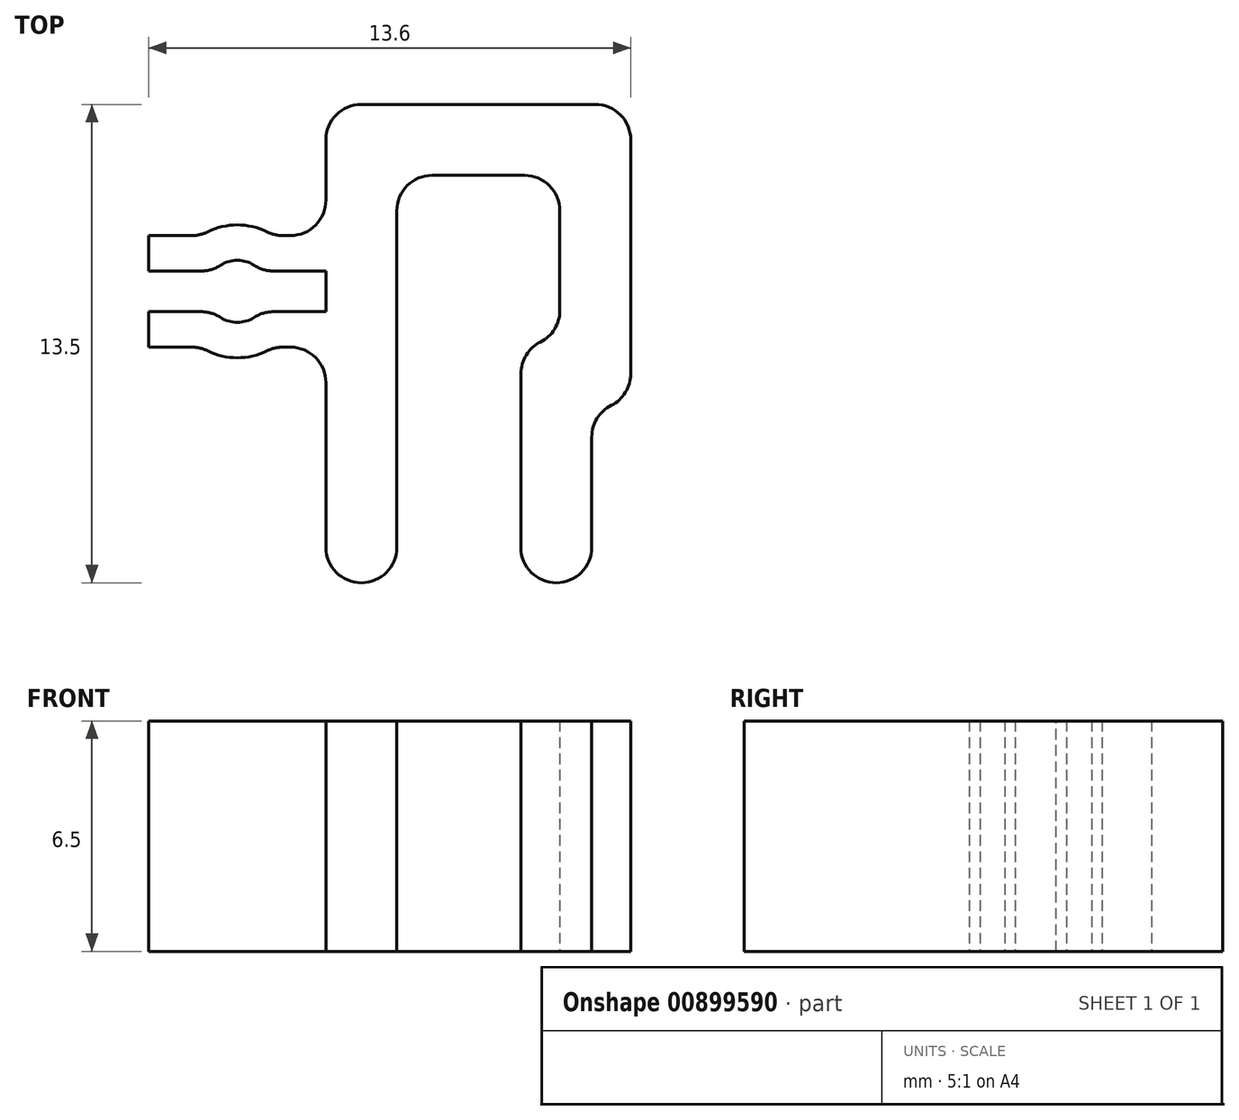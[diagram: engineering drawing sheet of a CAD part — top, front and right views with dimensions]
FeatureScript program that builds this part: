
annotation { "Feature Type Name" : "Feature", "Feature Type Description" : "" }
export const myFeature = defineFeature(function(context is Context, id is Id, definition is map)
    precondition{}
    {
        {
            var Q0;
            Q0=qCreatedBy(makeId("Top.planeOp"),FACE);
            var sketch = newSketch(context, id + "F0", { "sketchPlane" : qUnion([Q0])});
            skLineSegment(sketch, "E0.bottom", {"start": v(2.3, 2.3) * mm, "end": v(-2.3, 2.3) * mm});
            skLineSegment(sketch, "E0.left", {"start": v(2.3, 2.3) * mm, "end": v(2.3, -2.3) * mm});
            skLineSegment(sketch, "E0.right", {"start": v(-2.3, 2.3) * mm, "end": v(-2.3, -2.3) * mm});
            skPoint(sketch, "E0.middle", {"position": v(0, 0) * mm});
            skLineSegment(sketch, "E1.0", {"start": v(4.3, 4.3) * mm, "end": v(-4.3, 4.3) * mm});
            skLineSegment(sketch, "E1.1", {"start": v(4.3, 4.3) * mm, "end": v(4.3, -4.3) * mm});
            skLineSegment(sketch, "E2.0", {"start": v(-4.3, 4.3) * mm, "end": v(-4.3, -2.3) * mm});
            skLineSegment(sketch, "E3", {"start": v(2.3, -2.3) * mm, "end": v(1.2, -2.3) * mm});
            skLineSegment(sketch, "E4", {"start": v(1.2, -2.3) * mm, "end": v(1.2, -9.2) * mm});
            skLineSegment(sketch, "E5.0", {"start": v(3.2, -4.3) * mm, "end": v(3.2, -9.2) * mm});
            skLineSegment(sketch, "E6.0", {"start": v(4.3, -4.3) * mm, "end": v(3.2, -4.3) * mm});
            skLineSegment(sketch, "E7", {"start": v(1.2, -9.2) * mm, "end": v(3.2, -9.2) * mm});
            skLineSegment(sketch, "E8", {"start": v(-2.3, -2.3) * mm, "end": v(-2.3, -9.2) * mm});
            skLineSegment(sketch, "E9", {"start": v(-2.3, -9.2) * mm, "end": v(-4.3, -9.2) * mm});
            skLineSegment(sketch, "E10", {"start": v(-4.3, -9.2) * mm, "end": v(-4.3, -2.3) * mm});
            skLineSegment(sketch, "E11", {"start": v(-4.3, 0.6) * mm, "end": v(-5.78, 0.6) * mm});
            skLineSegment(sketch, "E12", {"start": v(-9.3, 0.6) * mm, "end": v(-9.3, -0.4) * mm});
            skLineSegment(sketch, "E13", {"start": v(-9.3, -0.4) * mm, "end": v(-7.46, -0.4) * mm});
            skLineSegment(sketch, "E14", {"start": v(-4.3, -1.55) * mm, "end": v(-6.14, -1.55) * mm});
            skLineSegment(sketch, "E15", {"start": v(-9.3, -1.55) * mm, "end": v(-9.3, -2.55) * mm});
            skLineSegment(sketch, "E16", {"start": v(-9.3, -2.55) * mm, "end": v(-4.3, -2.55) * mm});
            skLineSegment(sketch, "E17", {"start": v(-6.8, -0.4) * mm, "end": v(-6.8, -1.55) * mm, "construction": true});
            skArc(sketch, "E18", {"start": v(-7.46, -1.55) * mm, "mid": v(-6.8, -1.85) * mm, "end": v(-6.14, -1.55) * mm});
            skArc(sketch, "E19", {"start": v(-7.82, -2.55) * mm, "mid": v(-6.8, -2.85) * mm, "end": v(-5.78, -2.55) * mm});
            skArc(sketch, "E20.trimOffspring", {"start": v(-5.78, 0.6) * mm, "mid": v(-6.8, 0.9) * mm, "end": v(-7.82, 0.6) * mm});
            skLineSegment(sketch, "E21.trimOffspring", {"start": v(-7.82, 0.6) * mm, "end": v(-9.3, 0.6) * mm});
            skArc(sketch, "E22.trimOffspring", {"start": v(-6.14, -0.4) * mm, "mid": v(-6.8, -0.1) * mm, "end": v(-7.46, -0.4) * mm});
            skLineSegment(sketch, "E23.trimOffspring", {"start": v(-6.14, -0.4) * mm, "end": v(-4.3, -0.4) * mm});
            skLineSegment(sketch, "E24.trimOffspring", {"start": v(-7.46, -1.55) * mm, "end": v(-9.3, -1.55) * mm});
            skSolve(sketch);
        }
        {
            var Q0;
            Q0 = qSketchRegion(id + "F0", true);
            extrude(context, id + "F1", {"entities" : qUnion([Q0]), "depth" : 6.5 * mm, "offsetDistance" : 25.4 * mm});
        }
        {
            var Q0;
            {var subQ0=sQuery(id+"F0.wireOp",EDGE,"E19");var subQ1=sQuery(id+"F0.wireOp",EDGE,"E16");Q0=makeQuery(id+"F1.opExtrude","SWEPT_EDGE",EDGE,{"disambiguationData":[OSD([subQ1,subQ0]),TDD([makeQuery(id+"F0.imprint","INTERSECT",VERTEX,{"disambiguationData":[OD(0.0)],"derivedFrom":[subQ1,subQ0]})])]});}
            var Q1;
            {var subQ0=sQuery(id+"F0.wireOp",EDGE,"E19");var subQ1=sQuery(id+"F0.wireOp",EDGE,"E16");Q1=makeQuery(id+"F1.opExtrude","SWEPT_EDGE",EDGE,{"disambiguationData":[OSD([subQ1,subQ0]),TDD([makeQuery(id+"F0.imprint","INTERSECT",VERTEX,{"disambiguationData":[OD(1.0)],"derivedFrom":[subQ1,subQ0]})])]});}
            var Q2;
            Q2=makeQuery(id+"F1.opExtrude","SWEPT_EDGE",EDGE,{"disambiguationData":[OSD([sQuery(id+"F0.wireOp",EDGE,"E20.trimOffspring"),sQuery(id+"F0.wireOp",EDGE,"E21.trimOffspring")])]});
            var Q3;
            Q3=makeQuery(id+"F1.opExtrude","SWEPT_EDGE",EDGE,{"disambiguationData":[OSD([sQuery(id+"F0.wireOp",EDGE,"E11"),sQuery(id+"F0.wireOp",EDGE,"E20.trimOffspring")])]});
            fillet(context, id + "F2", {"entities" : qUnion([Q0, Q1, Q2, Q3]), "radius" : 1 * mm, "tangentPropagation" : true, "allowEdgeOverflow" : false});
        }
        {
            var Q0;
            Q0=makeQuery(id+"F1.opExtrude","SWEPT_EDGE",EDGE,{"disambiguationData":[OSD([sQuery(id+"F0.wireOp",EDGE,"E14"),sQuery(id+"F0.wireOp",EDGE,"E18")])]});
            var Q1;
            Q1=makeQuery(id+"F1.opExtrude","SWEPT_EDGE",EDGE,{"disambiguationData":[OSD([sQuery(id+"F0.wireOp",EDGE,"E18"),sQuery(id+"F0.wireOp",EDGE,"E24.trimOffspring")])]});
            var Q2;
            Q2=makeQuery(id+"F1.opExtrude","SWEPT_EDGE",EDGE,{"disambiguationData":[OSD([sQuery(id+"F0.wireOp",EDGE,"E13"),sQuery(id+"F0.wireOp",EDGE,"E22.trimOffspring")])]});
            var Q3;
            Q3=makeQuery(id+"F1.opExtrude","SWEPT_EDGE",EDGE,{"disambiguationData":[OSD([sQuery(id+"F0.wireOp",EDGE,"E22.trimOffspring"),sQuery(id+"F0.wireOp",EDGE,"E23.trimOffspring")])]});
            fillet(context, id + "F3", {"entities" : qUnion([Q0, Q1, Q2, Q3]), "radius" : 1 * mm, "tangentPropagation" : true, "allowEdgeOverflow" : false});
        }
        {
            var Q0;
            Q0=makeQuery(id+"F1.opExtrude","SWEPT_EDGE",EDGE,{"disambiguationData":[OSD([sQuery(id+"F0.wireOp",EDGE,"E9"),sQuery(id+"F0.wireOp",EDGE,"E10")])]});
            var Q1;
            Q1=makeQuery(id+"F1.opExtrude","SWEPT_EDGE",EDGE,{"disambiguationData":[OSD([sQuery(id+"F0.wireOp",EDGE,"E8"),sQuery(id+"F0.wireOp",EDGE,"E9")])]});
            var Q2;
            Q2=makeQuery(id+"F1.opExtrude","SWEPT_EDGE",EDGE,{"disambiguationData":[OSD([sQuery(id+"F0.wireOp",EDGE,"E4"),sQuery(id+"F0.wireOp",EDGE,"E7")])]});
            var Q3;
            Q3=makeQuery(id+"F1.opExtrude","SWEPT_EDGE",EDGE,{"disambiguationData":[OSD([sQuery(id+"F0.wireOp",EDGE,"E5.0"),sQuery(id+"F0.wireOp",EDGE,"E7")])]});
            var Q4;
            Q4=makeQuery(id+"F1.opExtrude","SWEPT_EDGE",EDGE,{"disambiguationData":[OSD([sQuery(id+"F0.wireOp",EDGE,"E1.0"),sQuery(id+"F0.wireOp",EDGE,"E2.0")])]});
            var Q5;
            Q5=makeQuery(id+"F1.opExtrude","SWEPT_EDGE",EDGE,{"disambiguationData":[OSD([sQuery(id+"F0.wireOp",EDGE,"E1.1"),sQuery(id+"F0.wireOp",EDGE,"E6.0")])]});
            var Q6;
            Q6=makeQuery(id+"F1.opExtrude","SWEPT_EDGE",EDGE,{"disambiguationData":[OSD([sQuery(id+"F0.wireOp",EDGE,"E1.0"),sQuery(id+"F0.wireOp",EDGE,"E1.1")])]});
            var Q7;
            Q7=makeQuery(id+"F1.opExtrude","SWEPT_EDGE",EDGE,{"disambiguationData":[OSD([sQuery(id+"F0.wireOp",EDGE,"E3"),sQuery(id+"F0.wireOp",EDGE,"E4")])]});
            fillet(context, id + "F4", {"entities" : qUnion([Q0, Q1, Q2, Q3, Q4, Q5, Q6, Q7]), "radius" : 1 * mm, "tangentPropagation" : true, "allowEdgeOverflow" : false});
        }
        {
            var Q0;
            Q0=makeQuery(id+"F1.opExtrude","SWEPT_EDGE",EDGE,{"disambiguationData":[OSD([sQuery(id+"F0.wireOp",EDGE,"E0.bottom"),sQuery(id+"F0.wireOp",EDGE,"E0.right")])]});
            var Q1;
            Q1=makeQuery(id+"F1.opExtrude","SWEPT_EDGE",EDGE,{"disambiguationData":[OSD([sQuery(id+"F0.wireOp",EDGE,"E0.bottom"),sQuery(id+"F0.wireOp",EDGE,"E0.left")])]});
            var Q2;
            Q2=makeQuery(id+"F1.opExtrude","SWEPT_EDGE",EDGE,{"disambiguationData":[OSD([sQuery(id+"F0.wireOp",EDGE,"E0.left"),sQuery(id+"F0.wireOp",EDGE,"E3")])]});
            var Q3;
            Q3=makeQuery(id+"F1.opExtrude","SWEPT_EDGE",EDGE,{"disambiguationData":[OSD([sQuery(id+"F0.wireOp",EDGE,"E5.0"),sQuery(id+"F0.wireOp",EDGE,"E6.0")])]});
            var Q4;
            Q4=makeQuery(id+"F1.opExtrude","SWEPT_EDGE",EDGE,{"disambiguationData":[OSD([sQuery(id+"F0.wireOp",EDGE,"E2.0"),sQuery(id+"F0.wireOp",EDGE,"E11")])]});
            var Q5;
            Q5=makeQuery(id+"F1.opExtrude","SWEPT_EDGE",EDGE,{"disambiguationData":[OSD([sQuery(id+"F0.wireOp",EDGE,"E10"),sQuery(id+"F0.wireOp",EDGE,"E16")])]});
            fillet(context, id + "F5", {"entities" : qUnion([Q0, Q1, Q2, Q3, Q4, Q5]), "radius" : 1 * mm, "tangentPropagation" : true, "allowEdgeOverflow" : false});
        }
    });
